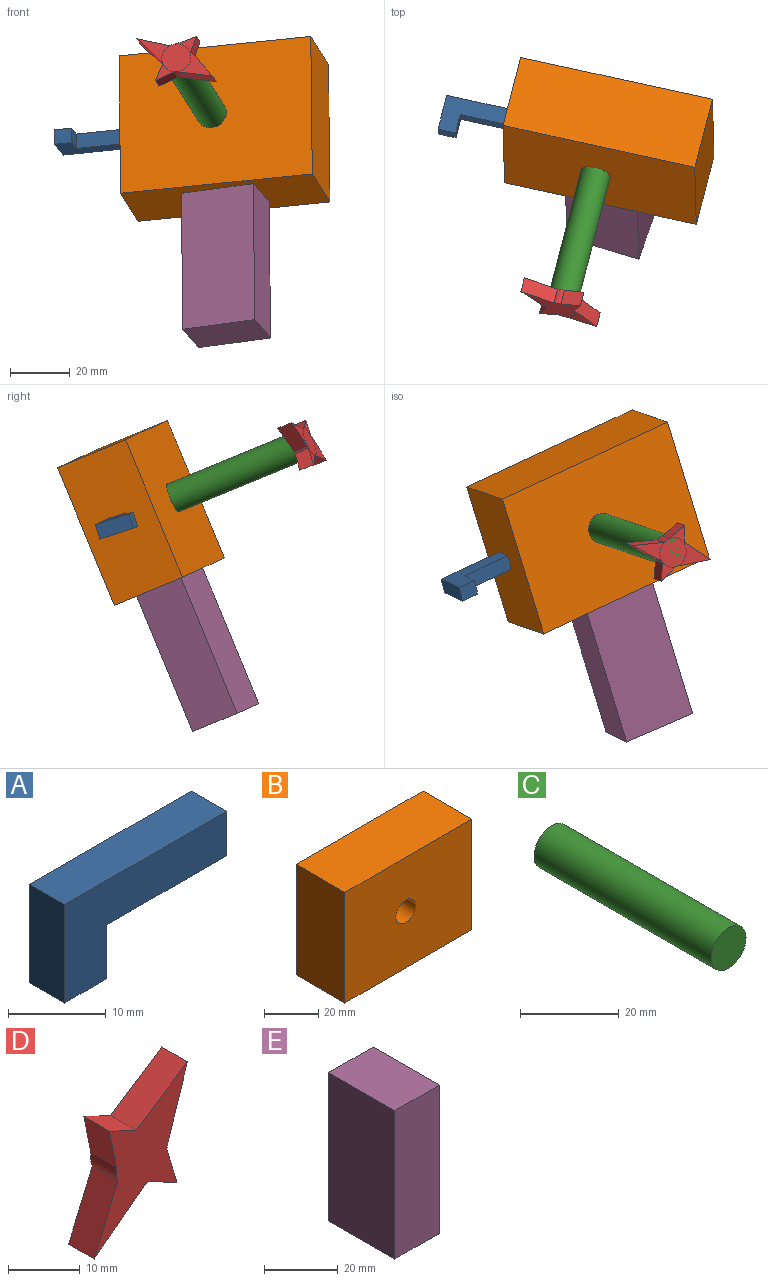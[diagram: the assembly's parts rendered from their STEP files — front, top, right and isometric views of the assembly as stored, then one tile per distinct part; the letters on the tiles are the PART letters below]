
ASSEMBLY  parts=5 mates=4
PART A: 8 faces, bbox 23.4x5.1x12.3 mm
  f0: plane 5.57x5.08mm, normal (1,0,0), area 28.3mm2, adj f1,f5,f6,f7
  f1: plane 23.38x5.08mm, normal (0,0,1), area 118.8mm2, adj f0,f2,f6,f7
  f2: plane 12.3x5.08mm, normal (-1,0,0), area 62.5mm2, adj f1,f3,f6,f7
  f3: plane 6.05x5.08mm, normal (0,0,-1), area 30.7mm2, adj f2,f4,f6,f7
  f4: plane 6.73x5.08mm, normal (1,0,0), area 34.2mm2, adj f3,f5,f6,f7
  f5: plane 17.33x5.08mm, normal (0,0,-1), area 88mm2, adj f0,f4,f6,f7
  f6: plane 23.38x12.3mm, normal (0,-1,0), area 170.9mm2, adj f0,f1,f2,f3,f4,f5
  f7: plane 23.38x12.3mm, normal (0,1,0), area 170.9mm2, adj f0,f1,f2,f3,f4,f5
PART B: 7 faces, bbox 66.2x25.4x49.9 mm
  f0: plane 49.93x25.4mm, normal (1,0,0), area 1268.3mm2, adj f1,f3,f5,f6
  f1: plane 66.17x25.4mm, normal (0,0,1), area 1680.7mm2, adj f0,f2,f5,f6
  f2: plane 49.93x25.4mm, normal (-1,0,0), area 1268.3mm2, adj f1,f3,f5,f6
  f3: plane 66.17x25.4mm, normal (0,0,-1), area 1680.7mm2, adj f0,f2,f5,f6
  f4: cylinder r=5.08mm len=25.4mm, axis (0,1,0), area 810.7mm2, adj f5,f6
  f5: plane 66.17x49.93mm, normal (0,-1,0), area 3222.9mm2, adj f0,f1,f2,f3,f4
  f6: plane 66.17x49.93mm, normal (0,1,0), area 3222.9mm2, adj f0,f1,f2,f3,f4
PART C: 3 faces, bbox 10x50.8x10 mm
  f0: cylinder r=5.02mm len=50.8mm, axis (0,1,0), area 1601.2mm2, adj f1,f2
  f1: plane 10.03x10.03mm, normal (0,-1,0), area 79.1mm2, adj f0
  f2: plane 10.03x10.03mm, normal (0,1,0), area 79.1mm2, adj f0
PART D: 13 faces, bbox 18.4x5.1x24.6 mm
  f0: plane 6.67x5.08mm, normal (0.96,0,0.28), area 35.3mm2, adj f1,f10,f11,f12
  f1: cylinder r=5.08mm len=5.08mm, axis (0,1,0), area 4.7mm2, adj f0,f2,f11,f12
  f2: plane 12.09x5.08mm, normal (0.95,0,-0.31), area 64.5mm2, adj f1,f3,f11,f12
  f3: plane 10.17x6.65mm, normal (-0.55,0,0.84), area 61.7mm2, adj f2,f4,f11,f12
  f4: plane 5.22x5.08mm, normal (0.42,0,0.91), area 29.3mm2, adj f3,f5,f11,f12
  f5: plane 6.88x5.08mm, normal (-0.98,0,-0.2), area 35.6mm2, adj f4,f6,f11,f12
  f6: cylinder r=5.08mm len=5.08mm, axis (0,1,0), area 12.6mm2, adj f5,f7,f11,f12
  f7: plane 11.02x5.08mm, normal (-0.92,0,0.39), area 60.8mm2, adj f6,f8,f11,f12
  f8: plane 10.07x7.73mm, normal (0.61,0,-0.79), area 64.5mm2, adj f7,f9,f11,f12
  f9: cylinder r=5.08mm len=5.08mm, axis (0,1,0), area 4mm2, adj f8,f10,f11,f12
  f10: plane 5.5x5.08mm, normal (-0.48,0,-0.88), area 31.8mm2, adj f0,f9,f11,f12
  f11: plane 24.56x18.41mm, normal (0,-1,0), area 177.3mm2, adj f0,f1,f2,f3,f4,f5,f6,f7
  f12: plane 24.56x18.41mm, normal (0,1,0), area 177.3mm2, adj f0,f1,f2,f3,f4,f5,f6,f7
PART E: 6 faces, bbox 17x25.4x49.4 mm
  f0: plane 25.4x17.03mm, normal (0,0,-1), area 432.6mm2, adj f1,f3,f4,f5
  f1: plane 49.4x25.4mm, normal (1,0,0), area 1254.8mm2, adj f0,f2,f4,f5
  f2: plane 25.4x17.03mm, normal (0,0,1), area 432.6mm2, adj f1,f3,f4,f5
  f3: plane 49.4x25.4mm, normal (-1,0,0), area 1254.8mm2, adj f0,f2,f4,f5
  f4: plane 49.4x17.03mm, normal (0,-1,0), area 841.4mm2, adj f0,f1,f2,f3
  f5: plane 49.4x17.03mm, normal (0,1,0), area 841.4mm2, adj f0,f1,f2,f3
PLACE A rot(axis=(-0.99,0.07,-0.13),108.3deg) t=(-120.19,7.24,6.25)mm
PLACE B rot(axis=(-0.85,-0.12,-0.51),26.1deg) t=(-56.1,-51.85,2.76)mm
PLACE C rot(axis=(-0.1,0.94,-0.32),85.4deg) t=(-33.07,-82.61,11.15)mm
PLACE D rot(axis=(-0.1,0.94,-0.32),85.4deg) t=(-134.69,-112.4,-1.75)mm
PLACE E rot(axis=(-0.26,0.18,0.95),74.9deg) t=(-94.15,-122.95,-21.67)mm
MATE revolute B.f3 <-> E.f2  axis (0.01,-0.38,-0.92) through (-66.27,-61.7,6.73)mm
MATE revolute C.f0 <-> B.f4  axis (0.23,0.9,-0.37) through (-70.84,-63.06,34.87)mm
MATE fastened D.f1 <-> C.f0  axis (-0.23,-0.9,0.37) through (-82.69,-108.74,53.67)mm
MATE revolute B.f2 <-> A.f0  axis (-0.97,0.21,-0.1) through (-98.69,-45.13,26.54)mm
